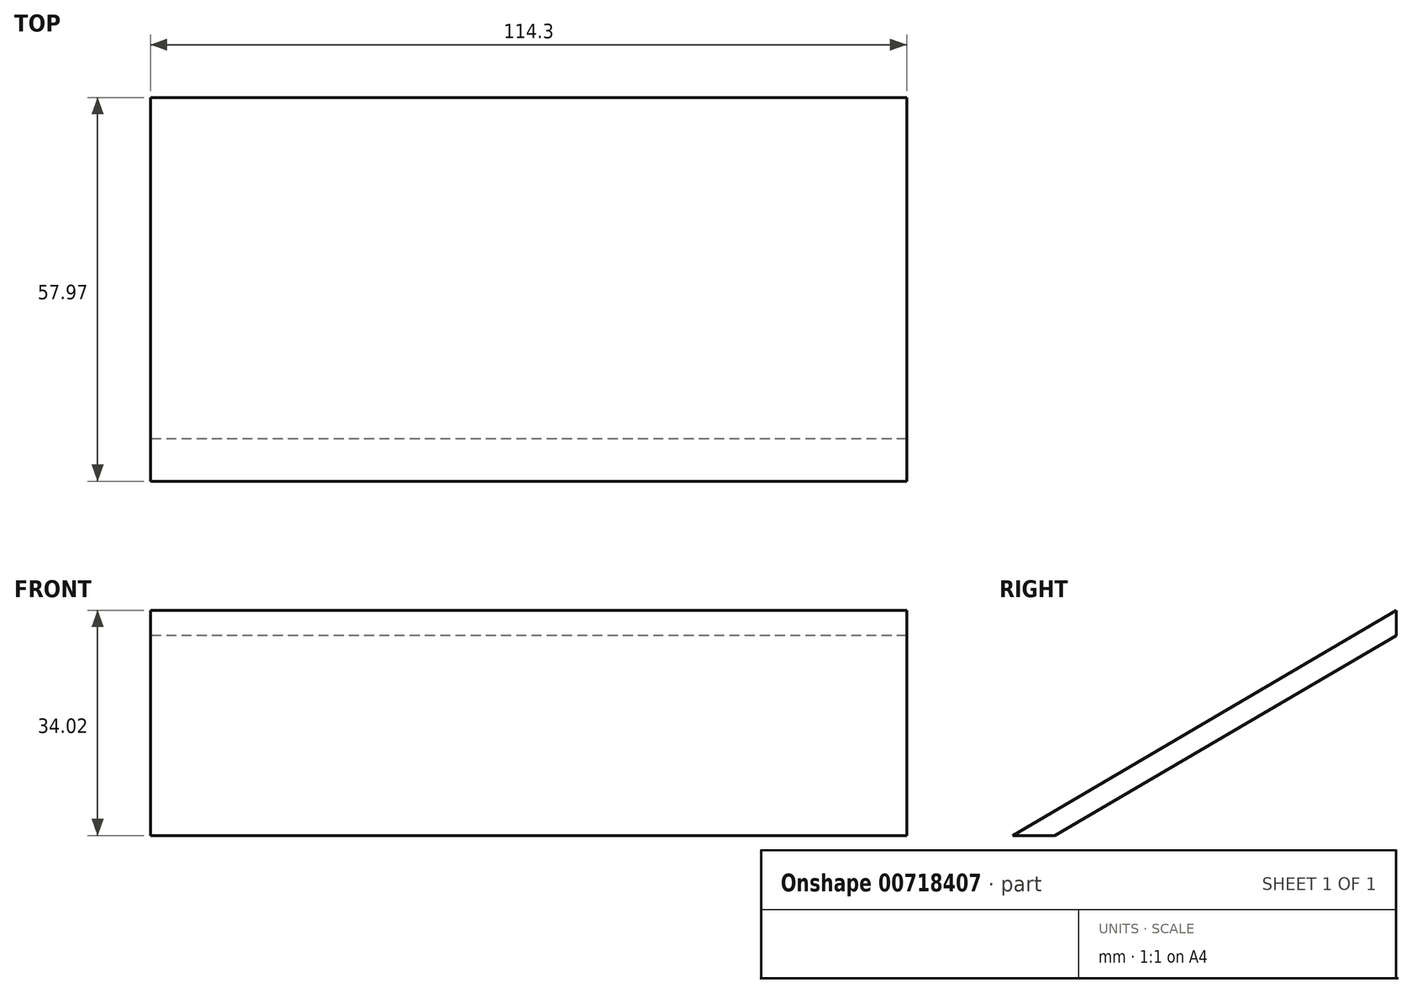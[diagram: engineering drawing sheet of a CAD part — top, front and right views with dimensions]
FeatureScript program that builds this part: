
annotation { "Feature Type Name" : "Feature", "Feature Type Description" : "" }
export const myFeature = defineFeature(function(context is Context, id is Id, definition is map)
    precondition{}
    {
        {
            var Q0;
            Q0=qCreatedBy(makeId("Right.planeOp"),FACE);
            var sketch = newSketch(context, id + "F0", { "sketchPlane" : qUnion([Q0])});
            skLineSegment(sketch, "E0", {"start": v(0, 30.2) * mm, "end": v(-51.6, 0) * mm});
            skLineSegment(sketch, "E1", {"start": v(-51.6, 0) * mm, "end": v(-57.97, 0) * mm});
            skLineSegment(sketch, "E2", {"start": v(-57.97, 0) * mm, "end": v(0, 34.02) * mm});
            skLineSegment(sketch, "E3", {"start": v(0, 34.02) * mm, "end": v(0, 30.2) * mm});
            skSolve(sketch);
        }
        {
            var Q0;
            Q0=makeQuery(id+"F0.imprint","IMPRINT",FACE,{"disambiguationData":[TD([[makeQuery(id+"F0.imprint","IMPRINT",EDGE,{"derivedFrom":sQuery(id+"F0.wireOp",EDGE,"E0")}),-1.0]])]});
            extrude(context, id + "F1", {"entities" : qUnion([Q0]), "endBound" : BoundingType.SYMMETRIC, "depth" : 114.3 * mm, "offsetDistance" : 25.4 * mm});
        }
    });
